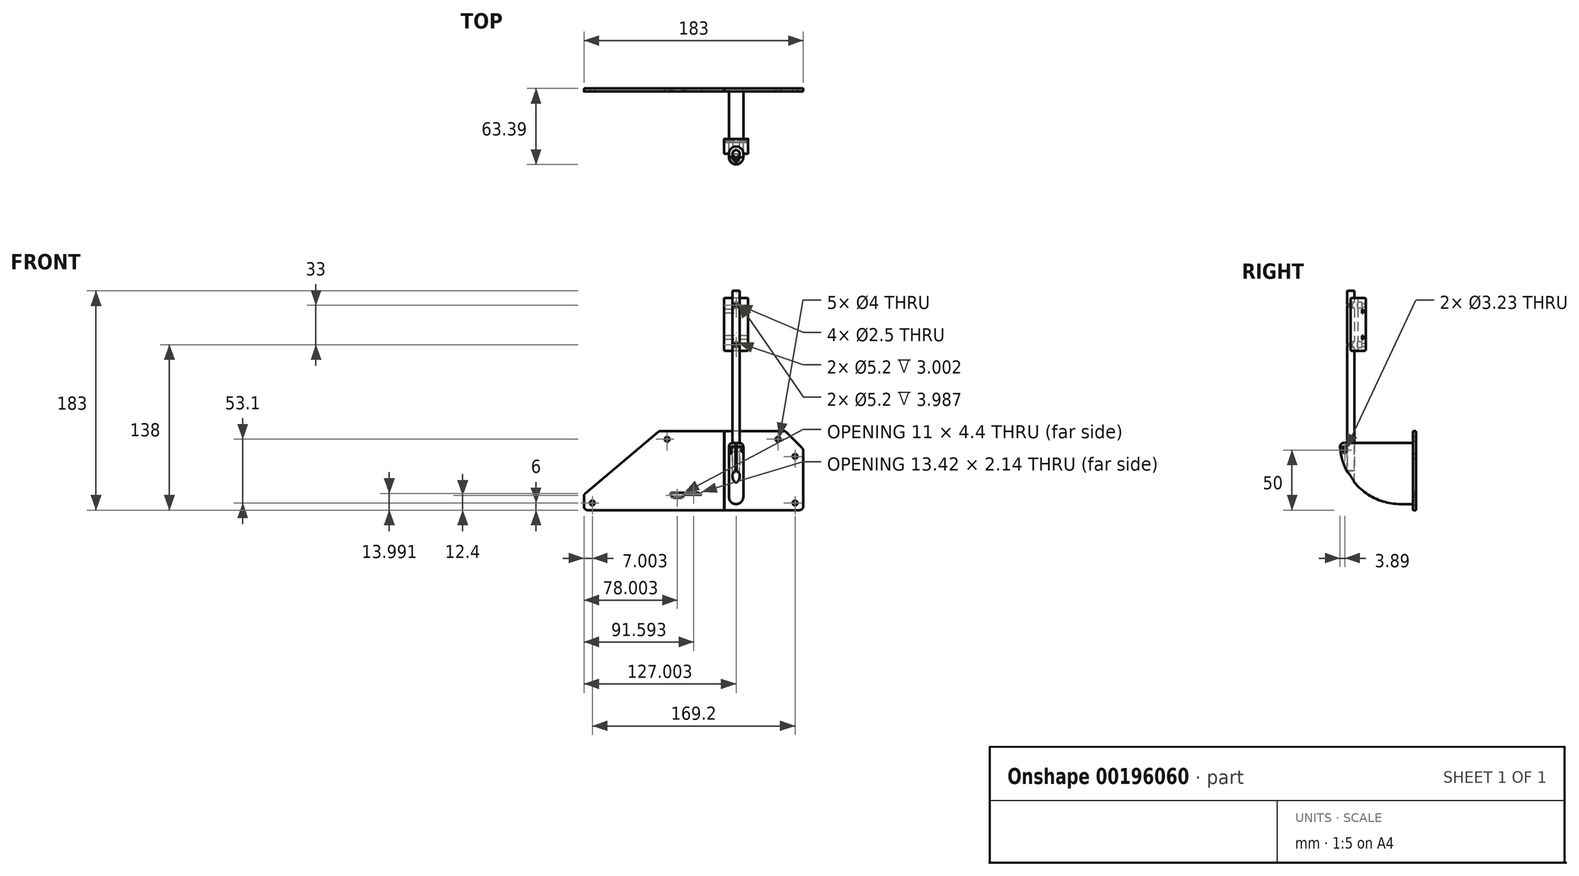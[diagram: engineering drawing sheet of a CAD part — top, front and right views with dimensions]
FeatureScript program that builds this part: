
annotation { "Feature Type Name" : "Feature", "Feature Type Description" : "" }
export const myFeature = defineFeature(function(context is Context, id is Id, definition is map)
    precondition{}
    {
        {
            var Q0;
            Q0=qCreatedBy(makeId("Front.planeOp"),FACE);
            var sketch = newSketch(context, id + "F0", { "sketchPlane" : qUnion([Q0])});
            skLineSegment(sketch, "E0.bottom", {"start": v(89.36, -33) * mm, "end": v(-93.64, -33) * mm});
            skLineSegment(sketch, "E0.top", {"start": v(89.36, 33) * mm, "end": v(-93.64, 33) * mm});
            skLineSegment(sketch, "E0.left", {"start": v(89.36, -33) * mm, "end": v(89.36, 33) * mm});
            skLineSegment(sketch, "E0.right", {"start": v(-93.64, -33) * mm, "end": v(-93.64, 33) * mm});
            skPoint(sketch, "E0.middle", {"position": v(-2.14, 0) * mm});
            skLineSegment(sketch, "E1", {"start": v(89.36, 18) * mm, "end": v(74.36, 33) * mm});
            skLineSegment(sketch, "E2", {"start": v(-93.64, -20) * mm, "end": v(-30.64, 33) * mm});
            skSolve(sketch);
        }
        {
            var Q0;
            {var subQ1=sQuery(id+"F0.wireOp",EDGE,"E0.bottom");Q0=makeQuery(id+"F0.imprint","IMPRINT",FACE,{"disambiguationData":[TD([[makeQuery(id+"F0.imprint","IMPRINT",EDGE,{"derivedFrom":subQ1}),-1.0]])]});}
            extrude(context, id + "F1", {"entities" : qUnion([Q0]), "depth" : 2.5 * mm});
        }
        {
            var Q0;
            Q0=makeQuery(id+"F1.opExtrude","CAP_FACE",FACE,{"disambiguationData":[OSD([sQuery(id+"F0.wireOp",EDGE,"E0.bottom"),sQuery(id+"F0.wireOp",EDGE,"E0.top"),sQuery(id+"F0.wireOp",EDGE,"E0.left"),sQuery(id+"F0.wireOp",EDGE,"E0.right"),sQuery(id+"F0.wireOp",EDGE,"E1"),sQuery(id+"F0.wireOp",EDGE,"E2")])],"isStart":false});
            var sketch = newSketch(context, id + "F2", { "sketchPlane" : qUnion([Q0])});
            skLineSegment(sketch, "E3", {"start": v(-24.14, 26.1) * mm, "end": v(68.36, 26.1) * mm});
            skLineSegment(sketch, "E4", {"start": v(82.56, 11.8) * mm, "end": v(82.56, -27) * mm});
            skLineSegment(sketch, "E5", {"start": v(82.56, -27) * mm, "end": v(-86.64, -27) * mm});
            skCircle(sketch, "E6", {"center": v(-24.14, 26.1) * mm, "radius": 2 * mm});
            skCircle(sketch, "E7", {"center": v(68.36, 26.1) * mm, "radius": 2 * mm});
            skCircle(sketch, "E8", {"center": v(82.56, 11.8) * mm, "radius": 2 * mm});
            skCircle(sketch, "E9", {"center": v(82.56, -27) * mm, "radius": 2 * mm});
            skCircle(sketch, "E10", {"center": v(-86.64, -27) * mm, "radius": 2 * mm});
            skLineSegment(sketch, "E11.bottom", {"start": v(4.66, -22.8) * mm, "end": v(-21.14, -22.8) * mm});
            skLineSegment(sketch, "E11.top", {"start": v(4.66, -17.7) * mm, "end": v(-21.14, -17.7) * mm});
            skLineSegment(sketch, "E11.left", {"start": v(4.66, -22.8) * mm, "end": v(4.66, -17.7) * mm});
            skLineSegment(sketch, "E11.right", {"start": v(-21.14, -22.8) * mm, "end": v(-21.14, -17.7) * mm});
            skLineSegment(sketch, "E12.bottom", {"start": v(4.66, -22.8) * mm, "end": v(-8.76, -22.8) * mm});
            skLineSegment(sketch, "E12.top", {"start": v(4.66, -20.08) * mm, "end": v(-8.76, -20.08) * mm});
            skLineSegment(sketch, "E12.left", {"start": v(4.66, -22.8) * mm, "end": v(4.66, -20.08) * mm});
            skLineSegment(sketch, "E12.right", {"start": v(-8.76, -22.8) * mm, "end": v(-8.76, -20.08) * mm});
            skArc(sketch, "E13", {"start": v(4.66, -20.08) * mm, "mid": v(-2.05, -17.94) * mm, "end": v(-8.76, -20.08) * mm});
            skLineSegment(sketch, "E14.bottom", {"start": v(-21.14, -22.8) * mm, "end": v(-10.14, -22.8) * mm});
            skLineSegment(sketch, "E14.top", {"start": v(-21.14, -18.4) * mm, "end": v(-10.14, -18.4) * mm});
            skLineSegment(sketch, "E14.left", {"start": v(-21.14, -22.8) * mm, "end": v(-21.14, -18.4) * mm});
            skLineSegment(sketch, "E14.right", {"start": v(-10.14, -22.8) * mm, "end": v(-10.14, -18.4) * mm});
            skLineSegment(sketch, "E15", {"start": v(-21.14, -21.2) * mm, "end": v(-19.24, -22.8) * mm});
            skLineSegment(sketch, "E16", {"start": v(-10.14, -21.2) * mm, "end": v(-12.04, -22.8) * mm});
            skSolve(sketch);
        }
        {
            var Q0;
            Q0=makeQuery(id+"F2.imprint","IMPRINT",FACE,{"disambiguationData":[TD([[makeQuery(id+"F2.imprint","IMPRINT",EDGE,{"derivedFrom":sQuery(id+"F2.wireOp",EDGE,"E6")}),1.0]])]});
            var Q1;
            Q1=makeQuery(id+"F2.imprint","IMPRINT",FACE,{"disambiguationData":[TD([[makeQuery(id+"F2.imprint","IMPRINT",EDGE,{"derivedFrom":sQuery(id+"F2.wireOp",EDGE,"E7")}),1.0]])]});
            var Q2;
            Q2=makeQuery(id+"F2.imprint","IMPRINT",FACE,{"disambiguationData":[TD([[makeQuery(id+"F2.imprint","IMPRINT",EDGE,{"derivedFrom":sQuery(id+"F2.wireOp",EDGE,"E8")}),1.0]])]});
            var Q3;
            Q3=makeQuery(id+"F2.imprint","IMPRINT",FACE,{"disambiguationData":[TD([[makeQuery(id+"F2.imprint","IMPRINT",EDGE,{"derivedFrom":sQuery(id+"F2.wireOp",EDGE,"E10")}),1.0]])]});
            var Q4;
            {var subQ0=sQuery(id+"F2.wireOp",EDGE,"E5");var subQ1=sQuery(id+"F2.wireOp",EDGE,"E4");var subQ2=makeQuery(id+"F2.imprint","INTERSECT",VERTEX,{"derivedFrom":[subQ1,subQ0]});Q4=makeQuery(id+"F2.imprint","IMPRINT",FACE,{"disambiguationData":[TD([[makeQuery(id+"F2.imprint","IMPRINT",EDGE,{"disambiguationData":[TD([[subQ2,1.0]])],"derivedFrom":subQ1}),-1.0]])]});}
            var Q5;
            {var subQ0=sQuery(id+"F2.wireOp",EDGE,"E5");var subQ1=sQuery(id+"F2.wireOp",EDGE,"E4");var subQ2=makeQuery(id+"F2.imprint","INTERSECT",VERTEX,{"derivedFrom":[subQ1,subQ0]});Q5=makeQuery(id+"F2.imprint","IMPRINT",FACE,{"disambiguationData":[TD([[makeQuery(id+"F2.imprint","IMPRINT",EDGE,{"disambiguationData":[TD([[subQ2,1.0]])],"derivedFrom":subQ1}),1.0]])]});}
            var Q6;
            Q6=makeQuery(id+"F2.imprint","IMPRINT",FACE,{"disambiguationData":[TD([[makeQuery(id+"F2.imprint","IMPRINT",EDGE,{"derivedFrom":sQuery(id+"F2.wireOp",EDGE,"E12.top")}),-1.0]])]});
            var Q7;
            Q7=makeQuery(id+"F2.imprint","IMPRINT",FACE,{"disambiguationData":[TD([[makeQuery(id+"F2.imprint","IMPRINT",EDGE,{"derivedFrom":sQuery(id+"F2.wireOp",EDGE,"E12.bottom")}),-1.0]])]});
            var Q8;
            {var subQ1=sQuery(id+"F2.wireOp",EDGE,"E14.top");Q8=makeQuery(id+"F2.imprint","IMPRINT",FACE,{"disambiguationData":[TD([[makeQuery(id+"F2.imprint","IMPRINT",EDGE,{"derivedFrom":subQ1}),-1.0]])]});}
            extrude(context, id + "F3", {"entities" : qUnion([Q0, Q1, Q2, Q3, Q4, Q5, Q6, Q7, Q8]), "operationType" : NewBodyOperationType.REMOVE, "endBound" : BoundingType.THROUGH_ALL, "oppositeDirection" : true, "depth" : 25 * mm});
        }
        {
            var Q0;
            Q0=makeQuery(id+"F1.opExtrude","CAP_FACE",FACE,{"disambiguationData":[OSD([sQuery(id+"F0.wireOp",EDGE,"E0.bottom"),sQuery(id+"F0.wireOp",EDGE,"E0.top"),sQuery(id+"F0.wireOp",EDGE,"E0.left"),sQuery(id+"F0.wireOp",EDGE,"E0.right"),sQuery(id+"F0.wireOp",EDGE,"E1"),sQuery(id+"F0.wireOp",EDGE,"E2")])],"isStart":false});
            var sketch = newSketch(context, id + "F4", { "sketchPlane" : qUnion([Q0])});
            skLineSegment(sketch, "E17", {"start": v(33.36, 23) * mm, "end": v(33.36, -22) * mm});
            skLineSegment(sketch, "E18.bottom", {"start": v(33.36, 23) * mm, "end": v(39.36, 23) * mm});
            skLineSegment(sketch, "E18.top", {"start": v(33.36, -22) * mm, "end": v(39.36, -22) * mm});
            skLineSegment(sketch, "E18.right", {"start": v(39.36, 23) * mm, "end": v(39.36, -22) * mm});
            skLineSegment(sketch, "E19.MirrorCS", {"start": v(27.36, 23) * mm, "end": v(27.36, -22) * mm});
            skLineSegment(sketch, "E20.MirrorCS", {"start": v(33.36, -22) * mm, "end": v(27.36, -22) * mm});
            skArc(sketch, "E21", {"start": v(27.36, -22) * mm, "mid": v(33.36, -28) * mm, "end": v(39.36, -22) * mm});
            skLineSegment(sketch, "E22", {"start": v(27.36, 23) * mm, "end": v(33.36, 23) * mm});
            skSolve(sketch);
        }
        {
            var Q0;
            Q0 = qSketchRegion(id + "F4", true);
            extrude(context, id + "F5", {"entities" : qUnion([Q0]), "operationType" : NewBodyOperationType.ADD, "depth" : 5 * mm});
        }
        {
            var Q0;
            Q0=makeQuery(id+"F5.opExtrude","CAP_EDGE",EDGE,{"disambiguationData":[OSD([sQuery(id+"F4.wireOp",EDGE,"E18.bottom"),sQuery(id+"F4.wireOp",EDGE,"E22")])],"isStart":true});
            var Q1;
            Q1=makeQuery(id+"F5.opExtrude","CAP_EDGE",EDGE,{"disambiguationData":[OSD([sQuery(id+"F4.wireOp",EDGE,"E19.MirrorCS")])],"isStart":true});
            var Q2;
            Q2=makeQuery(id+"F5.opExtrude","SWEPT_EDGE",EDGE,{"disambiguationData":[OSD([sQuery(id+"F4.wireOp",EDGE,"E19.MirrorCS"),sQuery(id+"F4.wireOp",EDGE,"E22")])]});
            var Q3;
            Q3=makeQuery(id+"F5.opExtrude","SWEPT_EDGE",EDGE,{"disambiguationData":[OSD([sQuery(id+"F4.wireOp",EDGE,"E18.bottom"),sQuery(id+"F4.wireOp",EDGE,"E18.right")])]});
            fillet(context, id + "F6", {"entities" : qUnion([Q0, Q1, Q2, Q3]), "radius" : 3 * mm, "tangentPropagation" : true, "allowEdgeOverflow" : false});
        }
        {
            var Q0;
            Q0=makeQuery(id+"F1.opExtrude","SWEPT_EDGE",EDGE,{"disambiguationData":[OSD([sQuery(id+"F0.wireOp",EDGE,"E0.bottom"),sQuery(id+"F0.wireOp",EDGE,"E0.right")])]});
            var Q1;
            Q1=makeQuery(id+"F1.opExtrude","SWEPT_EDGE",EDGE,{"disambiguationData":[OSD([sQuery(id+"F0.wireOp",EDGE,"E0.right"),sQuery(id+"F0.wireOp",EDGE,"E2")])]});
            var Q2;
            Q2=makeQuery(id+"F1.opExtrude","SWEPT_EDGE",EDGE,{"disambiguationData":[OSD([sQuery(id+"F0.wireOp",EDGE,"E0.top"),sQuery(id+"F0.wireOp",EDGE,"E2")])]});
            var Q3;
            Q3=makeQuery(id+"F1.opExtrude","SWEPT_EDGE",EDGE,{"disambiguationData":[OSD([sQuery(id+"F0.wireOp",EDGE,"E0.top"),sQuery(id+"F0.wireOp",EDGE,"E1")])]});
            var Q4;
            Q4=makeQuery(id+"F1.opExtrude","SWEPT_EDGE",EDGE,{"disambiguationData":[OSD([sQuery(id+"F0.wireOp",EDGE,"E0.left"),sQuery(id+"F0.wireOp",EDGE,"E1")])]});
            var Q5;
            Q5=makeQuery(id+"F1.opExtrude","SWEPT_EDGE",EDGE,{"disambiguationData":[OSD([sQuery(id+"F0.wireOp",EDGE,"E0.bottom"),sQuery(id+"F0.wireOp",EDGE,"E0.left")])]});
            fillet(context, id + "F7", {"entities" : qUnion([Q0, Q1, Q2, Q3, Q4, Q5]), "radius" : 3 * mm, "tangentPropagation" : true, "allowEdgeOverflow" : false});
        }
        {
            var Q0;
            Q0 = qSketchRegion(id + "F4", true);
            extrude(context, id + "F8", {"entities" : qUnion([Q0]), "operationType" : NewBodyOperationType.ADD, "depth" : 10 * mm});
        }
        {
            var Q0;
            Q0=makeQuery(id+"F8.opExtrude","CAP_FACE",FACE,{"disambiguationData":[OSD([sQuery(id+"F4.wireOp",EDGE,"E18.bottom"),sQuery(id+"F4.wireOp",EDGE,"E18.right"),sQuery(id+"F4.wireOp",EDGE,"E19.MirrorCS"),sQuery(id+"F4.wireOp",EDGE,"E21"),sQuery(id+"F4.wireOp",EDGE,"E22")])],"isStart":false});
            var Q1;
            Q1=makeQuery(id+"F8.opExtrude","CAP_EDGE",EDGE,{"disambiguationData":[OSD([sQuery(id+"F4.wireOp",EDGE,"E18.bottom"),sQuery(id+"F4.wireOp",EDGE,"E22")])],"isStart":false});
            revolve(context, id + "F9", {"operationType" : NewBodyOperationType.ADD, "entities" : qUnion([Q0]), "axis" : qUnion([Q1]), "revolveType" : RevolveType.ONE_DIRECTION, "oppositeDirection" : true, "angle" : 90 * degree});
        }
        {
            var Q0;
            {var subQ0=sQuery(id+"F4.wireOp",EDGE,"E18.bottom");var subQ1=sQuery(id+"F4.wireOp",EDGE,"070J427p-ooZk-l0iW-09gR-NElDgAndqo8N");Q0=makeQuery(id+"F9.boolean.opBoolean","MERGE",FACE,{"derivedFrom":[makeQuery(id+"F8.opExtrude","SWEPT_FACE",FACE,{"disambiguationData":[OSD([subQ1,subQ0])]}),makeQuery(id+"F9.opRevolve","CAP_FACE",FACE,{"disambiguationData":[OSD([subQ1,subQ0,sQuery(id+"F4.wireOp",EDGE,"E18.right"),sQuery(id+"F4.wireOp",EDGE,"E19.MirrorCS"),sQuery(id+"F4.wireOp",EDGE,"E21")])],"isStart":false})]});}
            var sketch = newSketch(context, id + "F10", { "sketchPlane" : qUnion([Q0])});
            skCircle(sketch, "E23", {"center": v(33.36, -54.5) * mm, "radius": 3.05 * mm});
            skLineSegment(sketch, "E24.bottom", {"start": v(32.9, -55.04) * mm, "end": v(33.83, -55.04) * mm});
            skLineSegment(sketch, "E24.top", {"start": v(32.9, -53.96) * mm, "end": v(33.83, -53.96) * mm});
            skLineSegment(sketch, "E24.left", {"start": v(32.9, -55.04) * mm, "end": v(32.9, -53.96) * mm});
            skLineSegment(sketch, "E24.right", {"start": v(33.83, -55.04) * mm, "end": v(33.83, -53.96) * mm});
            skLineSegment(sketch, "E25.bottom", {"start": v(33.83, -55.04) * mm, "end": v(32.9, -55.04) * mm});
            skLineSegment(sketch, "E25.top", {"start": v(33.83, -67.04) * mm, "end": v(32.9, -67.04) * mm});
            skLineSegment(sketch, "E25.left", {"start": v(33.83, -55.04) * mm, "end": v(33.83, -67.04) * mm});
            skLineSegment(sketch, "E25.right", {"start": v(32.9, -55.04) * mm, "end": v(32.9, -67.04) * mm});
            skSolve(sketch);
        }
        {
            var Q0;
            Q0 = qSketchRegion(id + "F10", true);
            var Q1;
            Q1=makeQuery(id+"F10.imprint","IMPRINT",FACE,{"disambiguationData":[TD([[makeQuery(id+"F10.imprint","IMPRINT",EDGE,{"derivedFrom":sQuery(id+"F10.wireOp",EDGE,"E24.top")}),-1.0]])]});
            extrude(context, id + "F11", {"entities" : qUnion([Q0, Q1]), "operationType" : NewBodyOperationType.REMOVE, "endBound" : BoundingType.THROUGH_ALL, "oppositeDirection" : true, "depth" : 25 * mm});
        }
        {
            var Q0;
            {var subQ0=sQuery(id+"F4.wireOp",EDGE,"E19.MirrorCS");Q0=makeQuery(id+"F9.boolean.opBoolean","MERGE",FACE,{"derivedFrom":[makeQuery(id+"F8.opExtrude","SWEPT_FACE",FACE,{"disambiguationData":[OSD([subQ0])]}),makeQuery(id+"F9.opRevolve","SWEPT_FACE",FACE,{"disambiguationData":[OSD([subQ0])]})]});}
            var sketch = newSketch(context, id + "F12", { "sketchPlane" : qUnion([Q0])});
            skCircle(sketch, "E26", {"center": v(59.5, 17) * mm, "radius": 1.61 * mm});
            skSolve(sketch);
        }
        {
            var Q0;
            Q0 = qSketchRegion(id + "F12", true);
            extrude(context, id + "F13", {"entities" : qUnion([Q0]), "operationType" : NewBodyOperationType.REMOVE, "endBound" : BoundingType.THROUGH_ALL, "oppositeDirection" : true, "depth" : 25 * mm});
        }
        {
            var Q0;
            {var subQ0=sQuery(id+"F4.wireOp",EDGE,"E19.MirrorCS");Q0=makeQuery(id+"F9.boolean.opBoolean","MERGE",FACE,{"derivedFrom":[makeQuery(id+"F8.opExtrude","SWEPT_FACE",FACE,{"disambiguationData":[OSD([subQ0])]}),makeQuery(id+"F9.opRevolve","SWEPT_FACE",FACE,{"disambiguationData":[OSD([subQ0])]})]});}
            var sketch = newSketch(context, id + "F14", { "sketchPlane" : qUnion([Q0])});
            skCircle(sketch, "E27.cCircle", {"center": v(59.5, 17) * mm, "radius": 2.73 * mm, "construction": true});
            skLineSegment(sketch, "E27.0", {"start": v(57.93, 19.73) * mm, "end": v(61.07, 19.73) * mm});
            skLineSegment(sketch, "E27.1", {"start": v(61.07, 19.73) * mm, "end": v(62.65, 17) * mm});
            skLineSegment(sketch, "E27.2", {"start": v(62.65, 17) * mm, "end": v(61.07, 14.28) * mm});
            skLineSegment(sketch, "E27.3", {"start": v(61.07, 14.27) * mm, "end": v(57.93, 14.27) * mm});
            skLineSegment(sketch, "E27.4", {"start": v(57.93, 14.27) * mm, "end": v(56.35, 17) * mm});
            skLineSegment(sketch, "E27.5", {"start": v(56.35, 17) * mm, "end": v(57.93, 19.72) * mm});
            skPoint(sketch, "E27.0.midPoint", {"position": v(59.5, 19.73) * mm});
            skSolve(sketch);
        }
        {
            var Q0;
            Q0 = qSketchRegion(id + "F14", true);
            extrude(context, id + "F15", {"entities" : qUnion([Q0]), "operationType" : NewBodyOperationType.REMOVE, "oppositeDirection" : true, "depth" : 2 * mm});
        }
        {
            var Q0;
            Q0=makeQuery(id+"F8.opExtrude","CAP_EDGE",EDGE,{"disambiguationData":[OSD([sQuery(id+"F4.wireOp",EDGE,"E18.bottom"),sQuery(id+"F4.wireOp",EDGE,"E22")])],"isStart":true});
            var Q1;
            Q1=makeQuery(id+"F8.opExtrude","CAP_EDGE",EDGE,{"disambiguationData":[OSD([sQuery(id+"F4.wireOp",EDGE,"E19.MirrorCS")])],"isStart":true});
            var Q2;
            {var subQ0=sQuery(id+"F4.wireOp",EDGE,"E19.MirrorCS");Q2=makeQuery(id+"F9.boolean.opBoolean","MERGE",EDGE,{"derivedFrom":[makeQuery(id+"F8.opExtrude","SWEPT_EDGE",EDGE,{"disambiguationData":[OSD([subQ0,sQuery(id+"F4.wireOp",EDGE,"E22")])]}),makeQuery(id+"F9.opRevolve","CAP_EDGE",EDGE,{"disambiguationData":[OSD([subQ0])],"isStart":false})]});}
            var Q3;
            {var subQ0=sQuery(id+"F4.wireOp",EDGE,"E18.right");Q3=makeQuery(id+"F9.boolean.opBoolean","MERGE",EDGE,{"derivedFrom":[makeQuery(id+"F8.opExtrude","SWEPT_EDGE",EDGE,{"disambiguationData":[OSD([sQuery(id+"F4.wireOp",EDGE,"E18.bottom"),subQ0])]}),makeQuery(id+"F9.opRevolve","CAP_EDGE",EDGE,{"disambiguationData":[OSD([subQ0])],"isStart":false})]});}
            fillet(context, id + "F16", {"entities" : qUnion([Q0, Q1, Q2, Q3]), "radius" : 3 * mm, "tangentPropagation" : true, "allowEdgeOverflow" : false});
        }
        {
            var Q0;
            Q0=qCreatedBy(makeId("Top.planeOp"),FACE);
            var sketch = newSketch(context, id + "F17", { "sketchPlane" : qUnion([Q0])});
            skCircle(sketch, "E28", {"center": v(33.36, -54.5) * mm, "radius": 3 * mm});
            skSolve(sketch);
        }
        {
            var Q0;
            Q0 = qSketchRegion(id + "F17", true);
            extrude(context, id + "F18", {"entities" : qUnion([Q0]), "depth" : 150 * mm});
        }
        {
            var Q0;
            Q0=makeQuery(id+"F18.opExtrude","CAP_EDGE",EDGE,{"disambiguationData":[OSD([sQuery(id+"F17.wireOp",EDGE,"E28")])],"isStart":false});
            var Q1;
            Q1=makeQuery(id+"F18.opExtrude","CAP_EDGE",EDGE,{"disambiguationData":[OSD([sQuery(id+"F17.wireOp",EDGE,"E28")])],"isStart":true});
            fillet(context, id + "F19", {"entities" : qUnion([Q0, Q1]), "radius" : .5 * mm, "tangentPropagation" : true, "allowEdgeOverflow" : false});
        }
        {
            var Q0;
            Q0=qCreatedBy(makeId("Top.planeOp"),FACE);
            cPlane(context, id + "F20", {"entities" : qUnion([Q0]), "cplaneType" : CPlaneType.OFFSET, "offset" : 100 * mm, "width" : 150 * mm, "height" : 150 * mm});
        }
        {
            var Q0;
            Q0=qCreatedBy(id+"F20.planeOp",FACE);
            var sketch = newSketch(context, id + "F21", { "sketchPlane" : qUnion([Q0])});
            skCircle(sketch, "E29", {"center": v(33.36, -54.5) * mm, "radius": 6.1 * mm});
            skLineSegment(sketch, "E30", {"start": v(43.36, -54.5) * mm, "end": v(43.36, -46) * mm});
            skLineSegment(sketch, "E31", {"start": v(23.36, -44) * mm, "end": v(23.36, -54.5) * mm});
            skLineSegment(sketch, "E32.top", {"start": v(23.36, -42) * mm, "end": v(43.36, -42) * mm});
            skLineSegment(sketch, "E32.left", {"start": v(23.36, -44) * mm, "end": v(23.36, -42) * mm});
            skArc(sketch, "E33", {"start": v(23.36, -54.5) * mm, "mid": v(33.36, -64.5) * mm, "end": v(43.36, -54.5) * mm});
            skLineSegment(sketch, "E34", {"start": v(43.36, -46) * mm, "end": v(43.36, -42) * mm});
            skLineSegment(sketch, "E35", {"start": v(33.36, -54.5) * mm, "end": v(43.36, -54.5) * mm});
            skLineSegment(sketch, "E36", {"start": v(33.36, -54.5) * mm, "end": v(23.36, -54.5) * mm});
            skSolve(sketch);
        }
        {
            var Q0;
            {var subQ1=sQuery(id+"F21.wireOp",EDGE,"E30");Q0=makeQuery(id+"F21.imprint","IMPRINT",FACE,{"disambiguationData":[TD([[makeQuery(id+"F21.imprint","IMPRINT",EDGE,{"derivedFrom":subQ1}),1.0]])]});}
            extrude(context, id + "F22", {"entities" : qUnion([Q0]), "depth" : 44 * mm});
        }
        {
            var Q0;
            Q0=makeQuery(id+"F22.opExtrude","SWEPT_FACE",FACE,{"disambiguationData":[OSD([sQuery(id+"F21.wireOp",EDGE,"E32.top")])]});
            var sketch = newSketch(context, id + "F23", { "sketchPlane" : qUnion([Q0])});
            skCircle(sketch, "E37", {"center": v(-33.36, 138) * mm, "radius": 1.25 * mm});
            skCircle(sketch, "E38", {"center": v(-33.36, 105) * mm, "radius": 1.25 * mm});
            skSolve(sketch);
        }
        {
            var Q0;
            Q0 = qSketchRegion(id + "F23", true);
            extrude(context, id + "F24", {"entities" : qUnion([Q0]), "operationType" : NewBodyOperationType.REMOVE, "endBound" : BoundingType.THROUGH_ALL, "oppositeDirection" : true, "depth" : 25 * mm});
        }
        {
            var Q0;
            Q0=makeQuery(id+"F22.opExtrude","CAP_FACE",FACE,{"disambiguationData":[OSD([sQuery(id+"F21.wireOp",EDGE,"E29"),sQuery(id+"F21.wireOp",EDGE,"dhfVceWs-B0XF-yq1A-NeCQ-ifYN0MqCLFIn"),sQuery(id+"F21.wireOp",EDGE,"E30"),sQuery(id+"F21.wireOp",EDGE,"E31"),sQuery(id+"F21.wireOp",EDGE,"E32.bottom"),sQuery(id+"F21.wireOp",EDGE,"E32.top"),sQuery(id+"F21.wireOp",EDGE,"E32.left"),sQuery(id+"F21.wireOp",EDGE,"E32.right")])],"isStart":false});
            var Q1;
            Q1=makeQuery(id+"F22.opExtrude","CAP_FACE",FACE,{"disambiguationData":[OSD([sQuery(id+"F21.wireOp",EDGE,"E29"),sQuery(id+"F21.wireOp",EDGE,"dhfVceWs-B0XF-yq1A-NeCQ-ifYN0MqCLFIn"),sQuery(id+"F21.wireOp",EDGE,"E30"),sQuery(id+"F21.wireOp",EDGE,"E31"),sQuery(id+"F21.wireOp",EDGE,"E32.bottom"),sQuery(id+"F21.wireOp",EDGE,"E32.top"),sQuery(id+"F21.wireOp",EDGE,"E32.left"),sQuery(id+"F21.wireOp",EDGE,"E32.right")])],"isStart":true});
            var Q2;
            Q2=makeQuery(id+"F22.opExtrude","SWEPT_EDGE",EDGE,{"disambiguationData":[OSD([sQuery(id+"F21.wireOp",EDGE,"E30"),sQuery(id+"F21.wireOp",EDGE,"E32.bottom")])]});
            var Q3;
            Q3=makeQuery(id+"F22.opExtrude","SWEPT_EDGE",EDGE,{"disambiguationData":[OSD([sQuery(id+"F21.wireOp",EDGE,"E31"),sQuery(id+"F21.wireOp",EDGE,"E33"),sQuery(id+"F21.wireOp",EDGE,"E36")])]});
            var Q4;
            Q4=makeQuery(id+"F22.opExtrude","SWEPT_EDGE",EDGE,{"disambiguationData":[OSD([sQuery(id+"F21.wireOp",EDGE,"E29"),sQuery(id+"F21.wireOp",EDGE,"E35")])]});
            var Q5;
            Q5=makeQuery(id+"F22.opExtrude","SWEPT_EDGE",EDGE,{"disambiguationData":[OSD([sQuery(id+"F21.wireOp",EDGE,"E29"),sQuery(id+"F21.wireOp",EDGE,"E36")])]});
            fillet(context, id + "F25", {"entities" : qUnion([Q0, Q1, Q2, Q3, Q4, Q5]), "radius" : .8 * mm, "tangentPropagation" : true, "allowEdgeOverflow" : false});
        }
        {
            var Q0;
            Q0=makeQuery(id+"F22.opExtrude","SWEPT_FACE",FACE,{"disambiguationData":[OSD([sQuery(id+"F21.wireOp",EDGE,"E35")])]});
            var sketch = newSketch(context, id + "F26", { "sketchPlane" : qUnion([Q0])});
            skCircle(sketch, "E39", {"center": v(33.36, 138) * mm, "radius": 2.6 * mm});
            skCircle(sketch, "E40", {"center": v(33.36, 105) * mm, "radius": 2.6 * mm});
            skSolve(sketch);
        }
        {
            var Q0;
            Q0 = qSketchRegion(id + "F26", true);
            extrude(context, id + "F27", {"entities" : qUnion([Q0]), "operationType" : NewBodyOperationType.REMOVE, "oppositeDirection" : true, "depth" : 9.5 * mm});
        }
        {
            var Q0;
            Q0=makeQuery(id+"F22.opExtrude","SWEPT_FACE",FACE,{"disambiguationData":[OSD([sQuery(id+"F21.wireOp",EDGE,"E31"),sQuery(id+"F21.wireOp",EDGE,"E32.left")])]});
            var sketch = newSketch(context, id + "F28", { "sketchPlane" : qUnion([Q0])});
            skLineSegment(sketch, "E41", {"start": v(54.5, 122) * mm, "end": v(42, 122) * mm});
            skLineSegment(sketch, "E42.bottom", {"start": v(45.15, 131.45) * mm, "end": v(44, 131.45) * mm});
            skLineSegment(sketch, "E42.top", {"start": v(45.15, 134.55) * mm, "end": v(44, 134.55) * mm});
            skLineSegment(sketch, "E42.left", {"start": v(45.15, 131.45) * mm, "end": v(45.15, 134.55) * mm});
            skLineSegment(sketch, "E42.right", {"start": v(44, 131.45) * mm, "end": v(44, 134.55) * mm});
            skPoint(sketch, "E42.middle", {"position": v(44.58, 133) * mm});
            skLineSegment(sketch, "E43.MirrorCS", {"start": v(45.15, 112.55) * mm, "end": v(45.15, 109.45) * mm});
            skLineSegment(sketch, "E44.MirrorCS", {"start": v(45.15, 109.45) * mm, "end": v(44, 109.45) * mm});
            skLineSegment(sketch, "E45.MirrorCS", {"start": v(44, 112.55) * mm, "end": v(44, 109.45) * mm});
            skLineSegment(sketch, "E46.MirrorCS", {"start": v(45.15, 112.55) * mm, "end": v(44, 112.55) * mm});
            skSolve(sketch);
        }
        {
            var Q0;
            Q0 = qSketchRegion(id + "F28", true);
            extrude(context, id + "F29", {"entities" : qUnion([Q0]), "operationType" : NewBodyOperationType.REMOVE, "endBound" : BoundingType.THROUGH_ALL, "oppositeDirection" : true, "depth" : 25 * mm});
        }
        {
            var Q0;
            Q0=makeQuery(id+"F1.opExtrude","CAP_FACE",FACE,{"disambiguationData":[OSD([sQuery(id+"F0.wireOp",EDGE,"E0.bottom"),sQuery(id+"F0.wireOp",EDGE,"E0.top"),sQuery(id+"F0.wireOp",EDGE,"E0.left"),sQuery(id+"F0.wireOp",EDGE,"E0.right"),sQuery(id+"F0.wireOp",EDGE,"E1"),sQuery(id+"F0.wireOp",EDGE,"E2")])],"isStart":false});
            var sketch = newSketch(context, id + "F30", { "sketchPlane" : qUnion([Q0])});
            skLineSegment(sketch, "E47.bottom", {"start": v(23.76, 35.47) * mm, "end": v(23.47, 35.47) * mm});
            skLineSegment(sketch, "E47.top", {"start": v(23.76, -37.01) * mm, "end": v(23.47, -37.01) * mm});
            skLineSegment(sketch, "E47.left", {"start": v(23.76, 35.47) * mm, "end": v(23.76, -37.01) * mm});
            skLineSegment(sketch, "E47.right", {"start": v(23.47, 35.47) * mm, "end": v(23.47, -37.01) * mm});
            skSolve(sketch);
        }
        {
            var Q0;
            Q0 = qSketchRegion(id + "F30", true);
            extrude(context, id + "F31", {"entities" : qUnion([Q0]), "operationType" : NewBodyOperationType.REMOVE, "endBound" : BoundingType.THROUGH_ALL, "oppositeDirection" : true, "depth" : 25 * mm});
        }
    });
